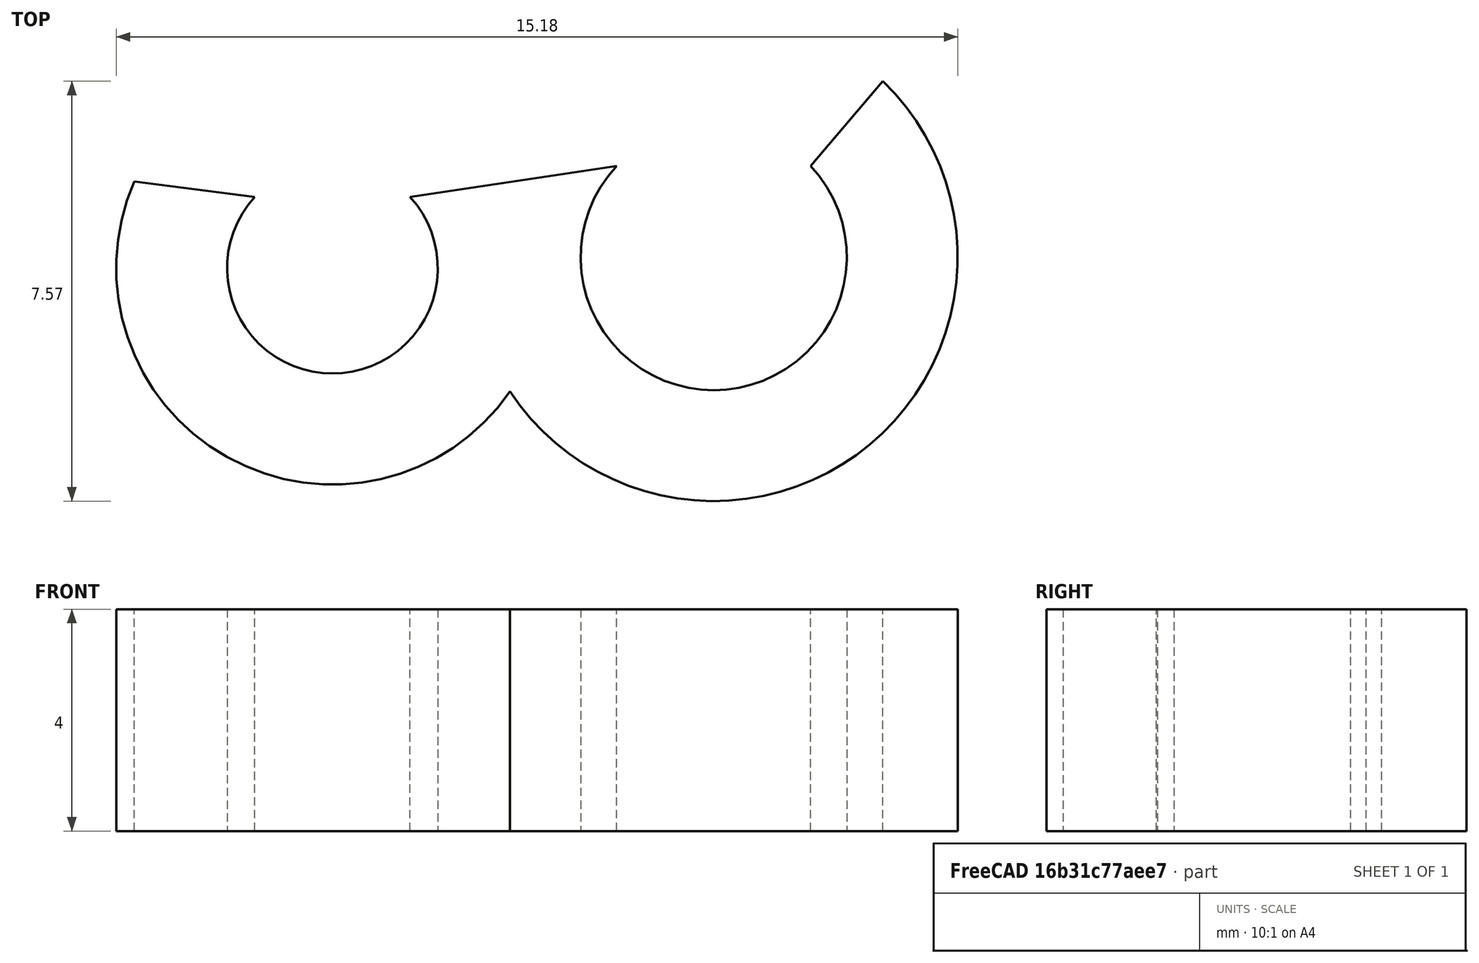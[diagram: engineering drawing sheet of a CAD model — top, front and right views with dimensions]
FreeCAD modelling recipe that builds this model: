
FCSTD DOCUMENT  (FreeCAD 0.17R13522 (Git))
Label: QiGan-jwei-2.1
License: All rights reserved
LicenseURL: http://en.wikipedia.org/wiki/All_rights_reserved
objects: Sketcher::SketchObject×1, PartDesign::Pad×1, PartDesign::Body×1
note: 4 computed .brp shape members not serialized (recipe doc carries the construction recipe); baked Part::Feature solids carry a one-line shape summary decoded from their .brp

FEATURE [Sketcher::SketchObject] Sketch
  MapMode = 5
  Support = -> [XY_Plane]
  sketch-geometry (7):
    g0: ArcOfCircle CenterX=0 CenterY=1 CenterZ=0 NormalX=0 NormalY=0 NormalZ=1 AngleXU=0 Radius=1.9 StartAngle=2.39918 EndAngle=7.02559
    g1: ArcOfCircle CenterX=6.8767 CenterY=1.2 CenterZ=0 NormalX=0 NormalY=0 NormalZ=1 AngleXU=0 Radius=2.4 StartAngle=2.3879 EndAngle=7.03688
    g2: ArcOfCircle CenterX=6.8767 CenterY=1.2 CenterZ=0 NormalX=0 NormalY=0 NormalZ=1 AngleXU=0 Radius=4.4 StartAngle=3.72487 EndAngle=7.08815
    g3: ArcOfCircle CenterX=0 CenterY=1 CenterZ=0 NormalX=0 NormalY=0 NormalZ=1 AngleXU=0 Radius=3.9 StartAngle=2.72866 EndAngle=5.67657
    g4: LineSegment StartX=-3.5722 StartY=2.56506 StartZ=0 EndX=-1.4 EndY=2.28452 EndZ=0
    g5: LineSegment StartX=1.4 StartY=2.28452 StartZ=0 EndX=5.1267 EndY=2.84241 EndZ=0
    g6: LineSegment StartX=8.6267 StartY=2.84241 StartZ=0 EndX=9.92651 EndY=4.37154 EndZ=0
  constraints (21):
    c: Radius(g0) = 1.9
    c: Distance(g0,g0) = 2.8
    c: Radius(g1) = 2.4
    c: Distance(g1,g1) = 3.5
    c: DistanceY(g-1,g1) = 1.2
    c: Coincident(g2,g1)
    c: Radius(g2) = 4.4
    c: Horizontal(g0,g0)
    c: Radius(g3) = 3.9
    c: Horizontal(g1,g1)
    c: Coincident(g3,g0)
    c: PointOnObject(g0,g-2)
    c: Distance(g-1,g0) = 1
    c: PointOnObject(g2,g3)
    c: Coincident(g3,g2)
    c: Coincident(g4,g3)
    c: Coincident(g4,g0)
    c: Coincident(g5,g0)
    c: Coincident(g5,g1)
    c: Coincident(g6,g1)
    c: Coincident(g6,g2)
FEATURE [PartDesign::Pad] Pad
  Length = 4
  Length2 = 100
  Profile = -> Sketch
  Type = 0
FEATURE [PartDesign::Body] Body
  Group = -> [Sketch,Pad]
  Origin = -> Origin
  Tip = -> Pad
